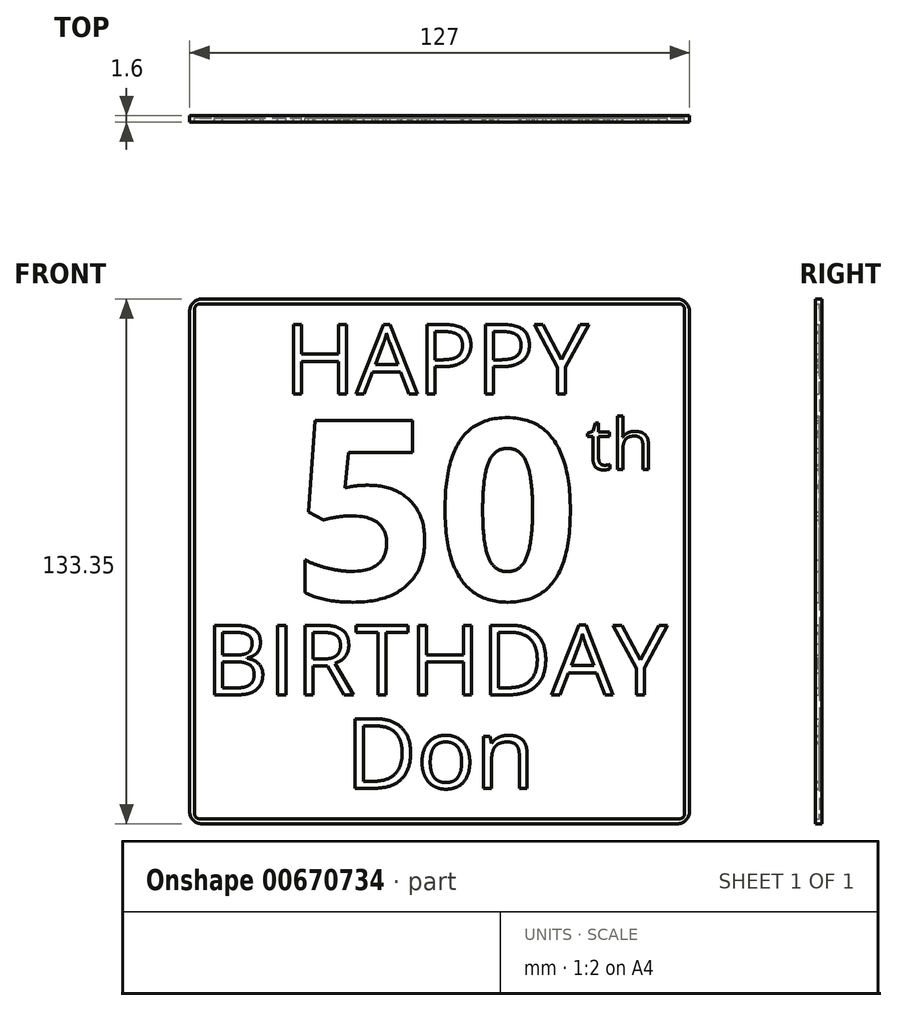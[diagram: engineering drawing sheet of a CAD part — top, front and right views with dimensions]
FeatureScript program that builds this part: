
annotation { "Feature Type Name" : "Feature", "Feature Type Description" : "" }
export const myFeature = defineFeature(function(context is Context, id is Id, definition is map)
    precondition{}
    {
        {
            var Q0;
            Q0=qCreatedBy(makeId("Front.planeOp"),FACE);
            var sketch = newSketch(context, id + "F0", { "sketchPlane" : qUnion([Q0])});
            skLineSegment(sketch, "E0.bottom", {"start": v(3.18, 0) * mm, "end": v(123.83, 0) * mm});
            skLineSegment(sketch, "E0.top", {"start": v(3.18, -133.35) * mm, "end": v(123.83, -133.35) * mm});
            skLineSegment(sketch, "E0.left", {"start": v(0, -3.17) * mm, "end": v(0, -130.18) * mm});
            skLineSegment(sketch, "E0.right", {"start": v(127, -3.17) * mm, "end": v(127, -130.18) * mm});
            skPoint(sketch, "E1.visualSharp", {"position": v(0, 0) * mm});
            skArc(sketch, "E1.filletArc", {"start": v(3.18, 0) * mm, "mid": v(0.93, -0.93) * mm, "end": v(0, -3.18) * mm});
            skPoint(sketch, "E2.visualSharp", {"position": v(127, 0) * mm});
            skArc(sketch, "E2.filletArc", {"start": v(127, -3.18) * mm, "mid": v(126.07, -0.93) * mm, "end": v(123.83, 0) * mm});
            skPoint(sketch, "E3.visualSharp", {"position": v(127, -133.35) * mm});
            skArc(sketch, "E3.filletArc", {"start": v(123.83, -133.35) * mm, "mid": v(126.07, -132.42) * mm, "end": v(127, -130.18) * mm});
            skPoint(sketch, "E4.visualSharp", {"position": v(0, -133.35) * mm});
            skArc(sketch, "E4.filletArc", {"start": v(0, -130.18) * mm, "mid": v(0.93, -132.42) * mm, "end": v(3.18, -133.35) * mm});
            skSolve(sketch);
        }
        {
            var Q0;
            Q0=qSketchRegion(id+"F0",true);
            extrude(context, id + "F1", {"entities" : qUnion([Q0]), "depth" : .6 * mm, "offsetDistance" : 25.4 * mm});
        }
        {
            var Q0;
            Q0=makeQuery(id+"F1.opExtrude","CAP_FACE",FACE,{"disambiguationData":[OSD([sQuery(id+"F0.wireOp",EDGE,"E0.bottom"),sQuery(id+"F0.wireOp",EDGE,"E0.top"),sQuery(id+"F0.wireOp",EDGE,"E0.left"),sQuery(id+"F0.wireOp",EDGE,"E0.right"),sQuery(id+"F0.wireOp",EDGE,"E1.filletArc"),sQuery(id+"F0.wireOp",EDGE,"E2.filletArc"),sQuery(id+"F0.wireOp",EDGE,"E3.filletArc"),sQuery(id+"F0.wireOp",EDGE,"E4.filletArc")])],"isStart":false});
            var sketch = newSketch(context, id + "F2", { "sketchPlane" : qUnion([Q0])});
            skText(sketch, "E5", { "text": "HAPPY", "fontName": "OpenSans-Regular.ttf"});
            skText(sketch, "E6", { "text": "BIRTHDAY", "fontName": "OpenSans-Regular.ttf"});
            skText(sketch, "E7", { "text": "50", "fontName": "OpenSans-Bold.ttf"});
            skText(sketch, "E8", { "text": "th", "fontName": "OpenSans-Regular.ttf"});
            skText(sketch, "E9", { "text": "Don", "fontName": "OpenSans-Regular.ttf"});
            skLineSegment(sketch, "E10", {"start": v(63.5, 0) * mm, "end": v(63.5, -6.35) * mm, "construction": true});
            skLineSegment(sketch, "E11", {"start": v(63.5, -24.13) * mm, "end": v(63.5, -30.48) * mm, "construction": true});
            skLineSegment(sketch, "E12", {"start": v(63.5, -76.4) * mm, "end": v(63.5, -82.76) * mm, "construction": true});
            skLineSegment(sketch, "E13", {"start": v(63.5, -100.54) * mm, "end": v(63.5, -106.53) * mm, "construction": true});
            skLineSegment(sketch, "E14", {"start": v(63.5, -124.3) * mm, "end": v(63.5, -129.53) * mm, "construction": true});
            skLineSegment(sketch, "E15", {"start": v(63.5, -147.31) * mm, "end": v(63.5, -133.35) * mm, "construction": true});
            const initialGuessF2  = {"E5": [0.024, -0.02413, 1, 0, 0.01778], "E6": [0.00395, -0.10054, 1, 0, 0.01778], "E7": [0.02616, -0.0764, 1, 0, 0.04593], "E8": [0.10084, -0.04326, 1, 0, 0.01278], "E9": [0.03965, -0.1243, 1, 0, 0.01778]};
            skSetInitialGuess(sketch, initialGuessF2);
            skSolve(sketch);
        }
        {
            var Q0;
            Q0=qSketchRegion(id+"F2",true);
            extrude(context, id + "F3", {"entities" : qUnion([Q0]), "operationType" : NewBodyOperationType.ADD, "depth" : 1 * mm, "offsetDistance" : 25.4 * mm});
        }
        {
            var Q0;
            {var subQ0=sQuery(id+"F0.wireOp",EDGE,"E2.filletArc");var subQ1=sQuery(id+"F0.wireOp",EDGE,"E0.bottom");var subQ2=sQuery(id+"F0.wireOp",EDGE,"E0.top");var subQ3=sQuery(id+"F0.wireOp",EDGE,"E0.left");var subQ4=sQuery(id+"F0.wireOp",EDGE,"E0.right");var subQ5=sQuery(id+"F0.wireOp",EDGE,"E1.filletArc");var subQ6=sQuery(id+"F0.wireOp",EDGE,"E3.filletArc");var subQ7=sQuery(id+"F0.wireOp",EDGE,"E4.filletArc");Q0=makeQuery(id+"F3.boolean.opBoolean","SPLIT",FACE,{"disambiguationData":[TD([makeQuery(id+"F1.opExtrude","SWEPT_FACE",FACE,{"disambiguationData":[OSD([subQ1])]})])],"derivedFrom":makeQuery(id+"F1.opExtrude","CAP_FACE",FACE,{"disambiguationData":[OSD([subQ1,subQ2,subQ3,subQ4,subQ5,subQ0,subQ6,subQ7])],"isStart":false})});}
            var sketch = newSketch(context, id + "F4", { "sketchPlane" : qUnion([Q0])});
            skLineSegment(sketch, "E16.0", {"start": v(127, -3.17) * mm, "end": v(127, -130.18) * mm});
            skLineSegment(sketch, "E16.1", {"start": v(3.18, -133.35) * mm, "end": v(123.83, -133.35) * mm});
            skLineSegment(sketch, "E16.2", {"start": v(0, -3.17) * mm, "end": v(0, -130.18) * mm});
            skLineSegment(sketch, "E16.3", {"start": v(3.18, 0) * mm, "end": v(123.83, 0) * mm});
            skArc(sketch, "E16.4", {"start": v(127, -3.18) * mm, "mid": v(126.07, -0.93) * mm, "end": v(123.83, 0) * mm});
            skArc(sketch, "E16.5", {"start": v(123.83, -133.35) * mm, "mid": v(126.07, -132.42) * mm, "end": v(127, -130.18) * mm});
            skArc(sketch, "E16.6", {"start": v(0, -130.18) * mm, "mid": v(0.93, -132.42) * mm, "end": v(3.18, -133.35) * mm});
            skArc(sketch, "E16.7", {"start": v(3.18, 0) * mm, "mid": v(0.93, -0.93) * mm, "end": v(0, -3.18) * mm});
            skLineSegment(sketch, "E17.0", {"start": v(2.54, -1.27) * mm, "end": v(124.46, -1.27) * mm});
            skLineSegment(sketch, "E17.1", {"start": v(1.27, -2.54) * mm, "end": v(1.27, -130.81) * mm});
            skLineSegment(sketch, "E17.2", {"start": v(2.54, -132.08) * mm, "end": v(124.46, -132.08) * mm});
            skLineSegment(sketch, "E17.3", {"start": v(125.73, -2.54) * mm, "end": v(125.73, -130.81) * mm});
            skPoint(sketch, "E18.visualSharp", {"position": v(125.73, -132.08) * mm});
            skArc(sketch, "E18.filletArc", {"start": v(124.46, -132.08) * mm, "mid": v(125.36, -131.7) * mm, "end": v(125.73, -130.81) * mm});
            skPoint(sketch, "E19.visualSharp", {"position": v(125.73, -1.27) * mm});
            skArc(sketch, "E19.filletArc", {"start": v(125.73, -2.54) * mm, "mid": v(125.36, -1.64) * mm, "end": v(124.46, -1.27) * mm});
            skPoint(sketch, "E20.visualSharp", {"position": v(1.27, -132.08) * mm});
            skArc(sketch, "E20.filletArc", {"start": v(1.27, -130.81) * mm, "mid": v(1.64, -131.7) * mm, "end": v(2.54, -132.08) * mm});
            skPoint(sketch, "E21.visualSharp", {"position": v(1.27, -1.27) * mm});
            skArc(sketch, "E21.filletArc", {"start": v(2.54, -1.27) * mm, "mid": v(1.64, -1.64) * mm, "end": v(1.27, -2.54) * mm});
            skSolve(sketch);
        }
        {
            var Q0;
            Q0 = qSketchRegion(id + "F4", true);
            extrude(context, id + "F5", {"entities" : qUnion([Q0]), "operationType" : NewBodyOperationType.ADD, "depth" : 1 * mm, "offsetDistance" : 25.4 * mm});
        }
    });
